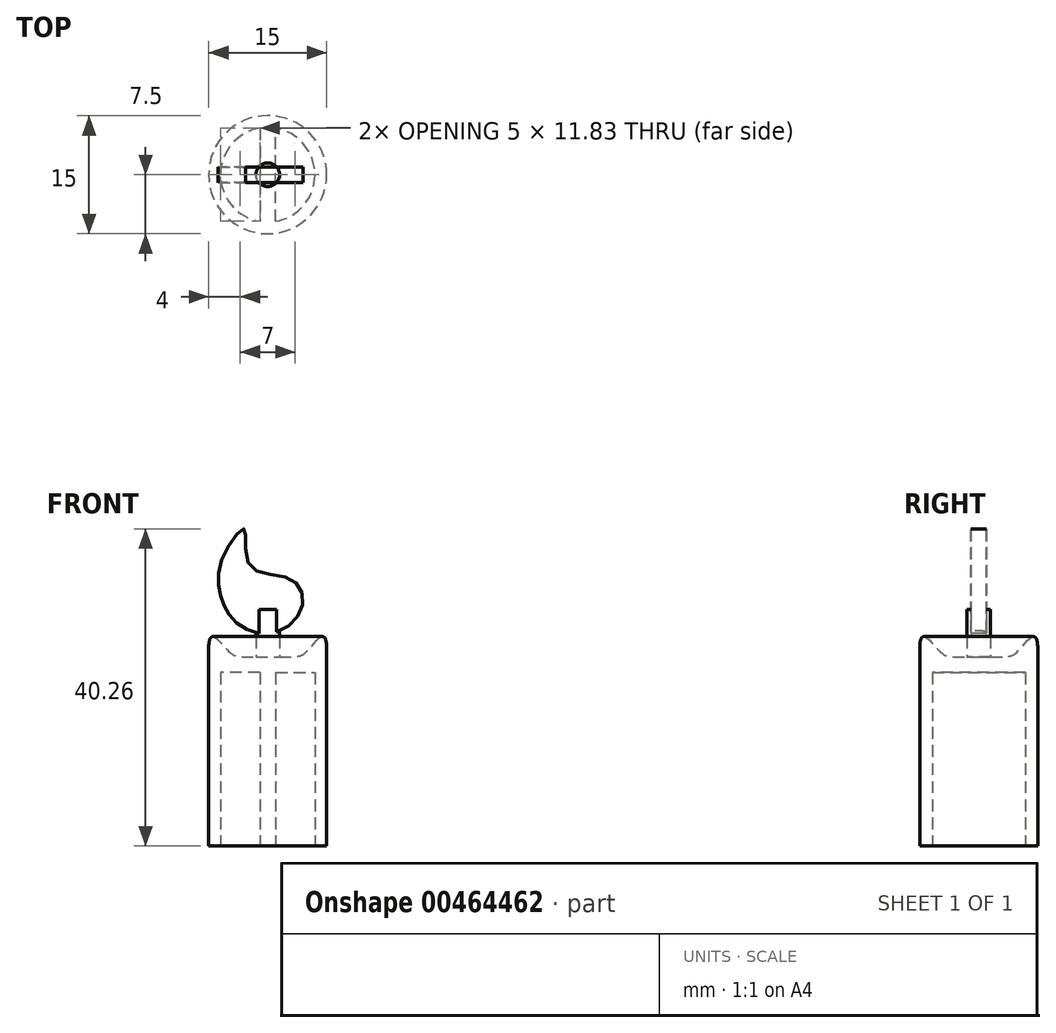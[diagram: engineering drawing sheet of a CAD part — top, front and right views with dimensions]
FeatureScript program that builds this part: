
annotation { "Feature Type Name" : "Feature", "Feature Type Description" : "" }
export const myFeature = defineFeature(function(context is Context, id is Id, definition is map)
    precondition{}
    {
        {
            var Q0;
            Q0=qCreatedBy(makeId("Front.planeOp"),FACE);
            var sketch = newSketch(context, id + "F0", { "sketchPlane" : qUnion([Q0])});
            skLineSegment(sketch, "E0.bottom", {"start": v(0, 0) * mm, "end": v(7.5, 0) * mm});
            skLineSegment(sketch, "E0.left", {"start": v(0, 0) * mm, "end": v(0, 25) * mm});
            skLineSegment(sketch, "E0.right", {"start": v(7.5, 0) * mm, "end": v(7.5, 25) * mm});
            skLineSegment(sketch, "E1.top", {"start": v(0, 30) * mm, "end": v(1.5, 30) * mm});
            skLineSegment(sketch, "E1.left", {"start": v(0, 25) * mm, "end": v(0, 30) * mm});
            skLineSegment(sketch, "E1.right", {"start": v(1.5, 24) * mm, "end": v(1.5, 30) * mm});
            skLineSegment(sketch, "E2", {"start": v(0, 25) * mm, "end": v(-7.5, 25) * mm, "construction": true});
            skLineSegment(sketch, "E3", {"start": v(0, 25) * mm, "end": v(7.5, 25) * mm, "construction": true});
            skFitSpline(sketch, "E4", {"points": [v(7.5, 25) * mm, v(5.61, 25.43) * mm, v(4.32, 24.23) * mm, v(1.5, 24) * mm], "startDerivative": vector(0, 25.92) * mm, "endDerivative": vector(-15.3, 0) * mm});
            skLineSegment(sketch, "E5", {"start": v(1.5, 24) * mm, "end": v(0, 24) * mm, "construction": true});
            skSolve(sketch);
        }
        {
            var Q0;
            Q0=qSketchRegion(id+"F0",true);
            var Q1;
            Q1=sQuery(id+"F0.wireOp",EDGE,"E0.left");
            revolve(context, id + "F1", {"entities" : qUnion([Q0]), "axis" : qUnion([Q1]), "revolveType" : RevolveType.FULL});
        }
        {
            var Q0;
            Q0=qCreatedBy(makeId("Front.planeOp"),FACE);
            var sketch = newSketch(context, id + "F2", { "sketchPlane" : qUnion([Q0])});
            skFitSpline(sketch, "E6", {"points": [v(0, 26.95) * mm, v(4.2, 29.85) * mm, v(3.18, 33.74) * mm, v(-2.37, 35.72) * mm, v(-2.95, 40.22) * mm, v(-5.8, 36.48) * mm, v(-6, 31.85) * mm, v(-4.4, 28.73) * mm, v(0, 26.95) * mm]});
            skSolve(sketch);
        }
        {
            var Q0;
            Q0=qSketchRegion(id+"F2",true);
            extrude(context, id + "F3", {"entities" : qUnion([Q0]), "operationType" : NewBodyOperationType.ADD, "endBound" : BoundingType.SYMMETRIC, "depth" : 2 * mm});
        }
        {
            var Q0;
            Q0=makeQuery(id+"F1.opRevolve","SWEPT_FACE",FACE,{"disambiguationData":[OSD([sQuery(id+"F0.wireOp",EDGE,"E0.bottom")])]});
            var sketch = newSketch(context, id + "F4", { "sketchPlane" : qUnion([Q0])});
            skArc(sketch, "E7", {"start": v(-1, 5.92) * mm, "mid": v(-6, 0) * mm, "end": v(-1, -5.92) * mm});
            skLineSegment(sketch, "E8", {"start": v(1, 5.92) * mm, "end": v(1, -5.92) * mm});
            skLineSegment(sketch, "E9", {"start": v(1, -5.92) * mm, "end": v(-1, -5.92) * mm, "construction": true});
            skLineSegment(sketch, "E10", {"start": v(-1, -5.92) * mm, "end": v(-1, 5.92) * mm});
            skArc(sketch, "E11.trimOffspring", {"start": v(1, -5.92) * mm, "mid": v(6, 0) * mm, "end": v(1, 5.92) * mm});
            skSolve(sketch);
        }
        {
            var Q0;
            Q0=qSketchRegion(id+"F4",true);
            extrude(context, id + "F5", {"entities" : qUnion([Q0]), "operationType" : NewBodyOperationType.REMOVE, "oppositeDirection" : true, "depth" : 22 * mm});
        }
        {
            var Q0;
            Q0=makeQuery(id+"F1.opRevolve","SWEPT_BODY",BODY,{"disambiguationData":[OSD([sQuery(id+"F0.wireOp",EDGE,"E0.bottom"),sQuery(id+"F0.wireOp",EDGE,"E0.left"),sQuery(id+"F0.wireOp",EDGE,"E0.right"),sQuery(id+"F0.wireOp",EDGE,"E1.top"),sQuery(id+"F0.wireOp",EDGE,"E1.left"),sQuery(id+"F0.wireOp",EDGE,"E1.right"),sQuery(id+"F0.wireOp",EDGE,"E4")])]});
            transform(context, id + "F6", {"entities" : qUnion([Q0]), "transformType" : TransformType.TRANSLATION_3D, "dx" : 0 * mm, "dy" : 0 * mm, "dz" : 0 * mm, "makeCopy" : true});
        }
    });
